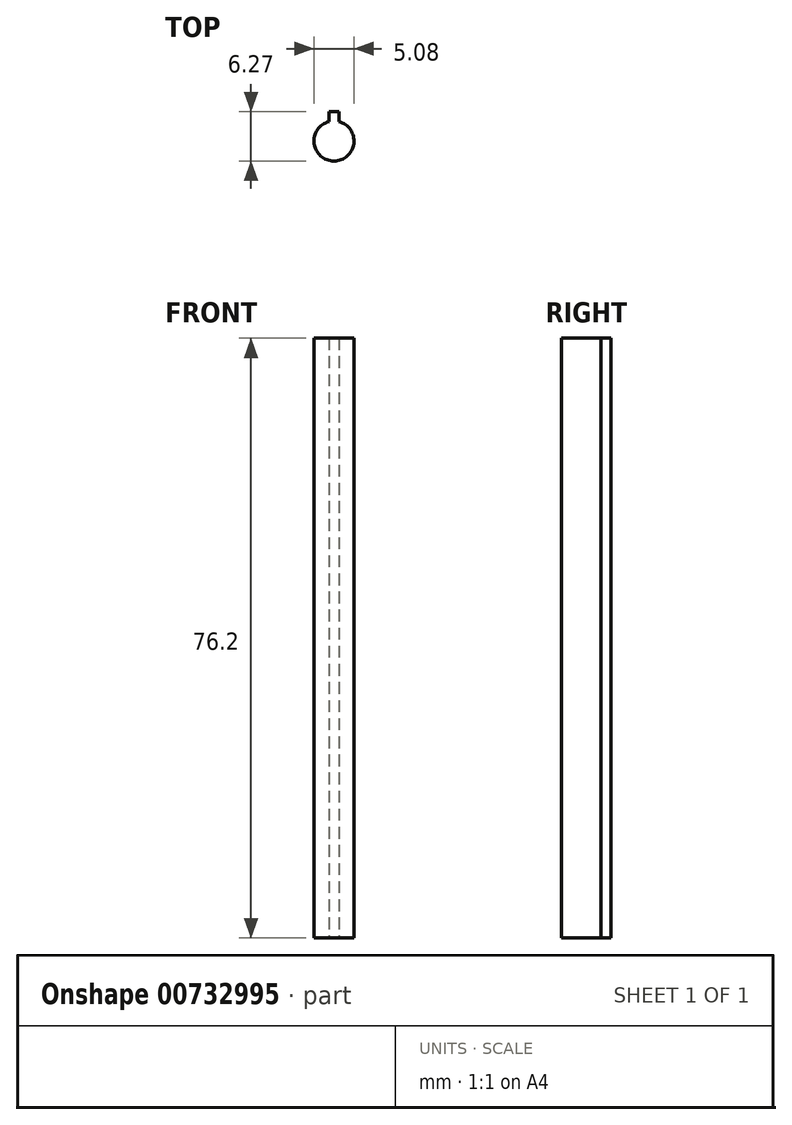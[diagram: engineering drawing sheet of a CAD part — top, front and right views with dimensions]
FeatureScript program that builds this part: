
annotation { "Feature Type Name" : "Feature", "Feature Type Description" : "" }
export const myFeature = defineFeature(function(context is Context, id is Id, definition is map)
    precondition{}
    {
        {
            var Q0;
            Q0=qCreatedBy(makeId("Top.planeOp"),FACE);
            var sketch = newSketch(context, id + "F0", { "sketchPlane" : qUnion([Q0])});
            skCircle(sketch, "E0", {"center": v(0, 0) * mm, "radius": 2.54 * mm});
            skLineSegment(sketch, "E1.bottom", {"start": v(-0.64, 2.46) * mm, "end": v(0.64, 2.46) * mm});
            skLineSegment(sketch, "E1.top", {"start": v(-0.64, 3.73) * mm, "end": v(0.64, 3.73) * mm});
            skLineSegment(sketch, "E1.left", {"start": v(-0.64, 2.46) * mm, "end": v(-0.64, 3.73) * mm});
            skLineSegment(sketch, "E1.right", {"start": v(0.64, 2.46) * mm, "end": v(0.64, 3.73) * mm});
            skSolve(sketch);
        }
        {
            var Q0;
            Q0 = qSketchRegion(id + "F0", true);
            extrude(context, id + "F1", {"entities" : qUnion([Q0]), "depth" : 76.2 * mm, "offsetDistance" : 25.4 * mm});
        }
    });
